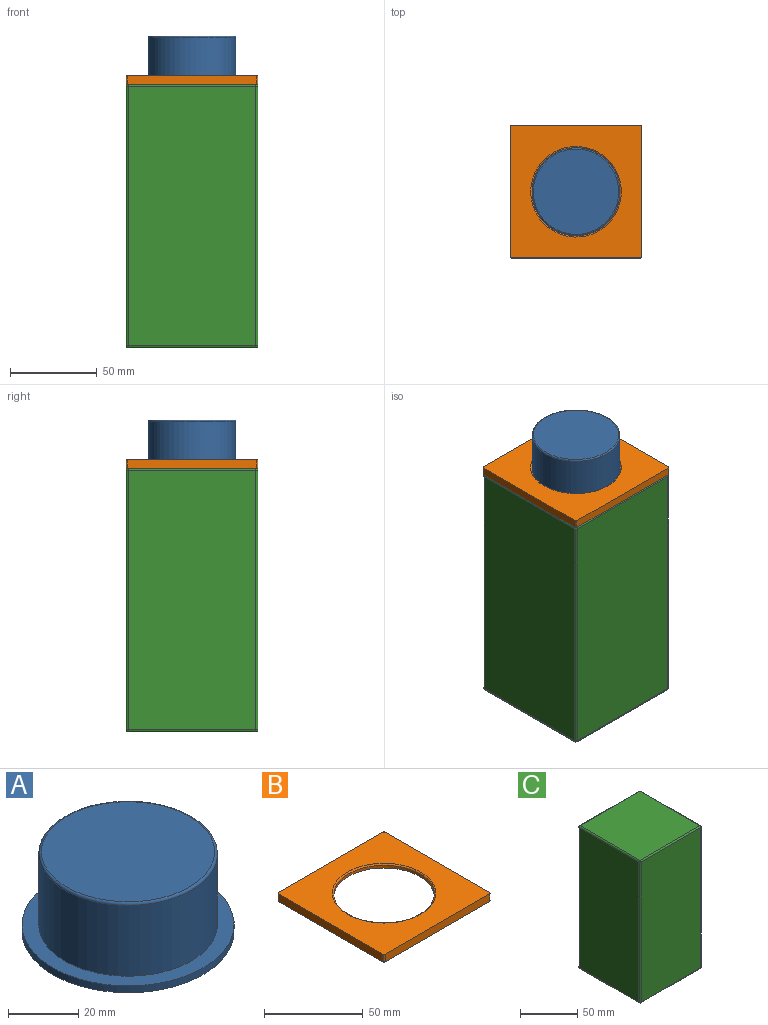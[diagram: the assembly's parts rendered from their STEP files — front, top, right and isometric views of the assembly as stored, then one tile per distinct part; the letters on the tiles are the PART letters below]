
ASSEMBLY  parts=3 mates=5
PART A: 6 faces, bbox 60.3x60.3x27.8 mm
  f0: cylinder r=30.16mm len=60.33mm, axis (0,0,-1), area 451.3mm2, adj f1,f2
  f1: plane 60.33x60.33mm, normal (0,0,1), area 831.3mm2, adj f0,f3
  f2: plane 60.33x60.33mm, normal (0,0,-1), area 2858.1mm2, adj f0
  f3: cylinder r=25.4mm len=50.8mm, axis (0,0,-1), area 3932.1mm2, adj f1,f5
  f4: plane 49.28x49.28mm, normal (0,0,1), area 1907mm2, adj f5
  f5: torus R=24.64mm, axis (0,0,1), area 188.9mm2, adj f3,f4
PART B: 14 faces, bbox 76.2x76.2x4.8 mm
  f0: cylinder r=25.4mm len=50.8mm, axis (0,0,-1), area 258.4mm2, adj f8,f13
  f1: plane 74.68x4.76mm, normal (0,1,0), area 355.6mm2, adj f5,f6,f9,f12
  f2: plane 74.68x4.76mm, normal (-1,0,0), area 355.6mm2, adj f5,f6,f9,f10
  f3: plane 74.68x4.76mm, normal (0,-1,0), area 355.6mm2, adj f5,f6,f10,f11
  f4: plane 74.68x4.76mm, normal (1,0,0), area 355.6mm2, adj f5,f6,f11,f12
  f5: plane 76.2x76.2mm, normal (0,0,1), area 3655.7mm2, adj f1,f2,f3,f4,f9,f10,f11,f12
  f6: plane 76.2x76.2mm, normal (0,0,-1), area 2947.8mm2, adj f1,f2,f3,f4,f7,f9,f10,f11
  f7: cylinder r=30.16mm len=60.33mm, axis (0,0,-1), area 451.3mm2, adj f6,f8
  f8: plane 60.33x60.33mm, normal (0,0,-1), area 831.3mm2, adj f0,f7
  f9: cylinder r=0.76mm len=4.76mm, axis (0,0,1), area 5.7mm2, adj f1,f2,f5,f6
  f10: cylinder r=0.76mm len=4.76mm, axis (0,0,-1), area 5.7mm2, adj f2,f3,f5,f6
  f11: cylinder r=0.76mm len=4.76mm, axis (0,0,1), area 5.7mm2, adj f3,f4,f5,f6
  f12: cylinder r=0.76mm len=4.76mm, axis (0,0,-1), area 5.7mm2, adj f1,f4,f5,f6
  f13: torus R=26.16mm, axis (0,0,1), area 193.1mm2, adj f0,f5
PART C: 26 faces, bbox 76.2x76.2x152.4 mm
  f0: plane 149.86x73.66mm, normal (0,1,0), area 11038.7mm2, adj f14,f19,f22,f25
  f1: plane 149.86x73.66mm, normal (-1,0,0), area 11038.7mm2, adj f11,f20,f21,f25
  f2: plane 149.86x73.66mm, normal (0,-1,0), area 11038.7mm2, adj f6,f10,f11,f12
  f3: plane 149.86x73.66mm, normal (1,0,0), area 11038.7mm2, adj f6,f9,f13,f14
  f4: plane 73.66x73.66mm, normal (0,0,1), area 5425.8mm2, adj f9,f10,f19,f20
  f5: plane 73.66x73.66mm, normal (0,0,-1), area 5425.8mm2, adj f12,f13,f21,f22
  f6: cylinder r=1.27mm len=149.86mm, axis (0,0,1), area 299mm2, adj f2,f3,f7,f8
  f7: sphere r=1.27mm, area 2.5mm2, adj f6,f9,f10
  f8: sphere r=1.27mm, area 2.5mm2, adj f6,f12,f13
  f9: cylinder r=1.27mm len=73.66mm, axis (0,-1,0), area 146.9mm2, adj f3,f4,f7,f15
  f10: cylinder r=1.27mm len=73.66mm, axis (-1,0,0), area 146.9mm2, adj f2,f4,f7,f16
  f11: cylinder r=1.27mm len=149.86mm, axis (0,0,-1), area 299mm2, adj f1,f2,f16,f17
  f12: cylinder r=1.27mm len=73.66mm, axis (1,0,0), area 146.9mm2, adj f2,f5,f8,f17
  f13: cylinder r=1.27mm len=73.66mm, axis (0,1,0), area 146.9mm2, adj f3,f5,f8,f18
  f14: cylinder r=1.27mm len=149.86mm, axis (0,0,-1), area 299mm2, adj f0,f3,f15,f18
  f15: sphere r=1.27mm, area 2.5mm2, adj f9,f14,f19
  f16: sphere r=1.27mm, area 2.5mm2, adj f10,f11,f20
  f17: sphere r=1.27mm, area 2.5mm2, adj f11,f12,f21
  f18: sphere r=1.27mm, area 2.5mm2, adj f13,f14,f22
  f19: cylinder r=1.27mm len=73.66mm, axis (1,0,0), area 146.9mm2, adj f0,f4,f15,f23
  f20: cylinder r=1.27mm len=73.66mm, axis (0,1,0), area 146.9mm2, adj f1,f4,f16,f23
  f21: cylinder r=1.27mm len=73.66mm, axis (0,-1,0), area 146.9mm2, adj f1,f5,f17,f24
  f22: cylinder r=1.27mm len=73.66mm, axis (-1,0,0), area 146.9mm2, adj f0,f5,f18,f24
  f23: sphere r=1.27mm, area 2.5mm2, adj f19,f20,f25
  f24: sphere r=1.27mm, area 2.5mm2, adj f21,f22,f25
  f25: cylinder r=1.27mm len=149.86mm, axis (0,0,1), area 299mm2, adj f0,f1,f23,f24
PLACE A t=(54.51,-28.49,-44.74)mm
PLACE B t=(22.86,-10.3,-44.74)mm
PLACE C t=(35.32,-15.21,-197.14)mm
MATE planar A.f0 <-> B.f0  axis (0,0,1) through (38.72,-18.37,-42.35)mm
MATE planar C.f3 <-> B.f4  axis (1,0,0) through (76.82,-18.37,-120.94)mm
MATE planar C.f4 <-> A.f0  axis (0,0,1) through (38.72,-18.37,-44.74)mm
MATE planar B.f3 <-> C.f2  axis (0,-1,0) through (38.72,-56.47,-42.35)mm
MATE revolute B.f0 <-> A.f0  axis (0,0,-1) through (38.72,-18.37,-44.74)mm
